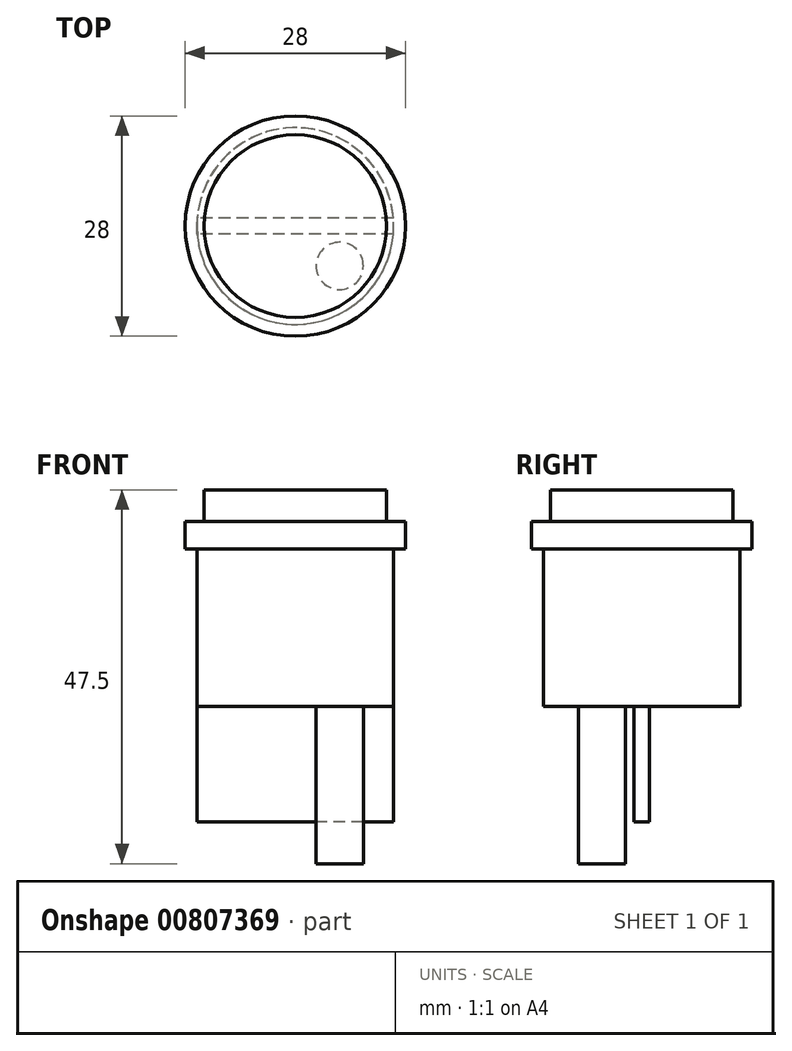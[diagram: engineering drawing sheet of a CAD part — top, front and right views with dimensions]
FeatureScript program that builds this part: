
annotation { "Feature Type Name" : "Feature", "Feature Type Description" : "" }
export const myFeature = defineFeature(function(context is Context, id is Id, definition is map)
    precondition{}
    {
        {
            var Q0;
            Q0=qCreatedBy(makeId("Top.planeOp"),FACE);
            var sketch = newSketch(context, id + "F0", { "sketchPlane" : qUnion([Q0])});
            skCircle(sketch, "E0", {"center": v(0, 0) * mm, "radius": 14 * mm});
            skSolve(sketch);
        }
        {
            var Q0;
            Q0 = qSketchRegion(id + "F0", true);
            extrude(context, id + "F1", {"entities" : qUnion([Q0]), "depth" : 3.5 * mm, "offsetDistance" : 25 * mm});
        }
        {
            var Q0;
            Q0=makeQuery(id+"F1.opExtrude","CAP_FACE",FACE,{"disambiguationData":[OSD([sQuery(id+"F0.wireOp",EDGE,"E0")])],"isStart":true});
            var sketch = newSketch(context, id + "F2", { "sketchPlane" : qUnion([Q0])});
            skCircle(sketch, "E1", {"center": v(0, 0) * mm, "radius": 12.5 * mm});
            skSolve(sketch);
        }
        {
            var Q0;
            Q0 = qSketchRegion(id + "F2", true);
            extrude(context, id + "F3", {"entities" : qUnion([Q0]), "operationType" : NewBodyOperationType.ADD, "depth" : (34.7 - 14.7) * mm, "offsetDistance" : 25 * mm});
        }
        {
            var Q0;
            Q0=makeQuery(id+"F3.opExtrude","CAP_FACE",FACE,{"disambiguationData":[OSD([sQuery(id+"F2.wireOp",EDGE,"E1")])],"isStart":false});
            var sketch = newSketch(context, id + "F4", { "sketchPlane" : qUnion([Q0])});
            skLineSegment(sketch, "E2.bottom", {"start": v(12.46, 1) * mm, "end": v(-12.46, 1) * mm});
            skLineSegment(sketch, "E2.top", {"start": v(12.46, -1) * mm, "end": v(-12.46, -1) * mm});
            skLineSegment(sketch, "E2.left", {"start": v(12.46, 1) * mm, "end": v(12.46, -1) * mm});
            skLineSegment(sketch, "E2.right", {"start": v(-12.46, 1) * mm, "end": v(-12.46, -1) * mm});
            skPoint(sketch, "E2.middle", {"position": v(0, 0) * mm});
            skSolve(sketch);
        }
        {
            var Q0;
            Q0 = qSketchRegion(id + "F4", true);
            extrude(context, id + "F5", {"entities" : qUnion([Q0]), "operationType" : NewBodyOperationType.ADD, "depth" : 14.7 * mm, "offsetDistance" : 25 * mm});
        }
        {
            var Q0;
            Q0=makeQuery(id+"F1.opExtrude","CAP_FACE",FACE,{"disambiguationData":[OSD([sQuery(id+"F0.wireOp",EDGE,"E0")])],"isStart":false});
            var sketch = newSketch(context, id + "F6", { "sketchPlane" : qUnion([Q0])});
            skCircle(sketch, "E3", {"center": v(0, 0) * mm, "radius": 11.6 * mm});
            skSolve(sketch);
        }
        {
            var Q0;
            Q0 = qSketchRegion(id + "F6", true);
            extrude(context, id + "F7", {"entities" : qUnion([Q0]), "depth" : 4 * mm, "offsetDistance" : 25 * mm});
        }
        {
            var Q0;
            {var subQ0=sQuery(id+"F2.wireOp",EDGE,"E1");var subQ1=makeQuery(id+"F3.opExtrude","CAP_FACE",FACE,{"disambiguationData":[OSD([subQ0])],"isStart":false});Q0=makeQuery(id+"F5.boolean.opBoolean","SPLIT",FACE,{"disambiguationData":[TD([makeQuery(id+"F3.opExtrude","SWEPT_FACE",FACE,{"disambiguationData":[OSD([subQ0])]}),subQ1,makeQuery(id+"F5.opExtrude","SWEPT_FACE",FACE,{"disambiguationData":[OSD([sQuery(id+"F4.wireOp",EDGE,"E2.bottom")])]}),makeQuery(id+"F5.opExtrude","SWEPT_FACE",FACE,{"disambiguationData":[OSD([sQuery(id+"F4.wireOp",EDGE,"E2.left")])]}),makeQuery(id+"F5.opExtrude","SWEPT_FACE",FACE,{"disambiguationData":[OSD([sQuery(id+"F4.wireOp",EDGE,"E2.right")])]})])],"derivedFrom":subQ1});}
            var sketch = newSketch(context, id + "F8", { "sketchPlane" : qUnion([Q0])});
            skCircle(sketch, "E4", {"center": v(5.64, 5.06) * mm, "radius": 3 * mm});
            skSolve(sketch);
        }
        {
            var Q0;
            Q0 = qSketchRegion(id + "F8", true);
            extrude(context, id + "F9", {"entities" : qUnion([Q0]), "depth" : 20 * mm, "offsetDistance" : 25 * mm});
        }
    });
